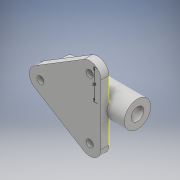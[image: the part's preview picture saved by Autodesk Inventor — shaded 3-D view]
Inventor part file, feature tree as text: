
AUTODESK INVENTOR PART (.ipt)
format: ipt  version: 2018 (Build 220112000, 112)  size: 156,160 bytes
history: native  units: mm
features: sketch x6, extrude x5
ambient origin geometry x8: Origin, YZ Plane, XZ Plane, XY Plane, X Axis, Y Axis, Z Axis, Center Point
bodies: Solid1 (feature_tree)
feature tree (11):
  extrude  "Extrusion1"  Depth=10.0mm
  extrude  "Extrusion2"  Depth=10.0mm
  sketch  "Sketch8"  dims[d40=76.0mm d41=62.0mm]
  extrude  "Extrusion6"  Depth=76.0mm
  extrude  "Extrusion7"  Depth=9.0mm
  extrude  "Extrusion8"  Depth=38.0mm
  sketch  "Sketch1"  dims[d8=10.0mm d9=0.0mm d10=9.0mm]
  sketch  "Sketch2"  dims[d15=10.0mm d16=0.0mm d37=62.0mm]
  sketch  "Sketch9"  dims[d42=9.0mm d43=9.0mm]
  sketch  "Sketch10"  dims[d44=62.0mm d45=38.0mm]
  sketch  "Sketch11"  dims[d46=24.0mm d47=33.0mm d48=70.0mm d49=0.0mm d50=22.0mm d51=0.0mm d52=16.0mm d53=70.0mm d54=0.0mm d29=1.0mm d30=1.0mm]
